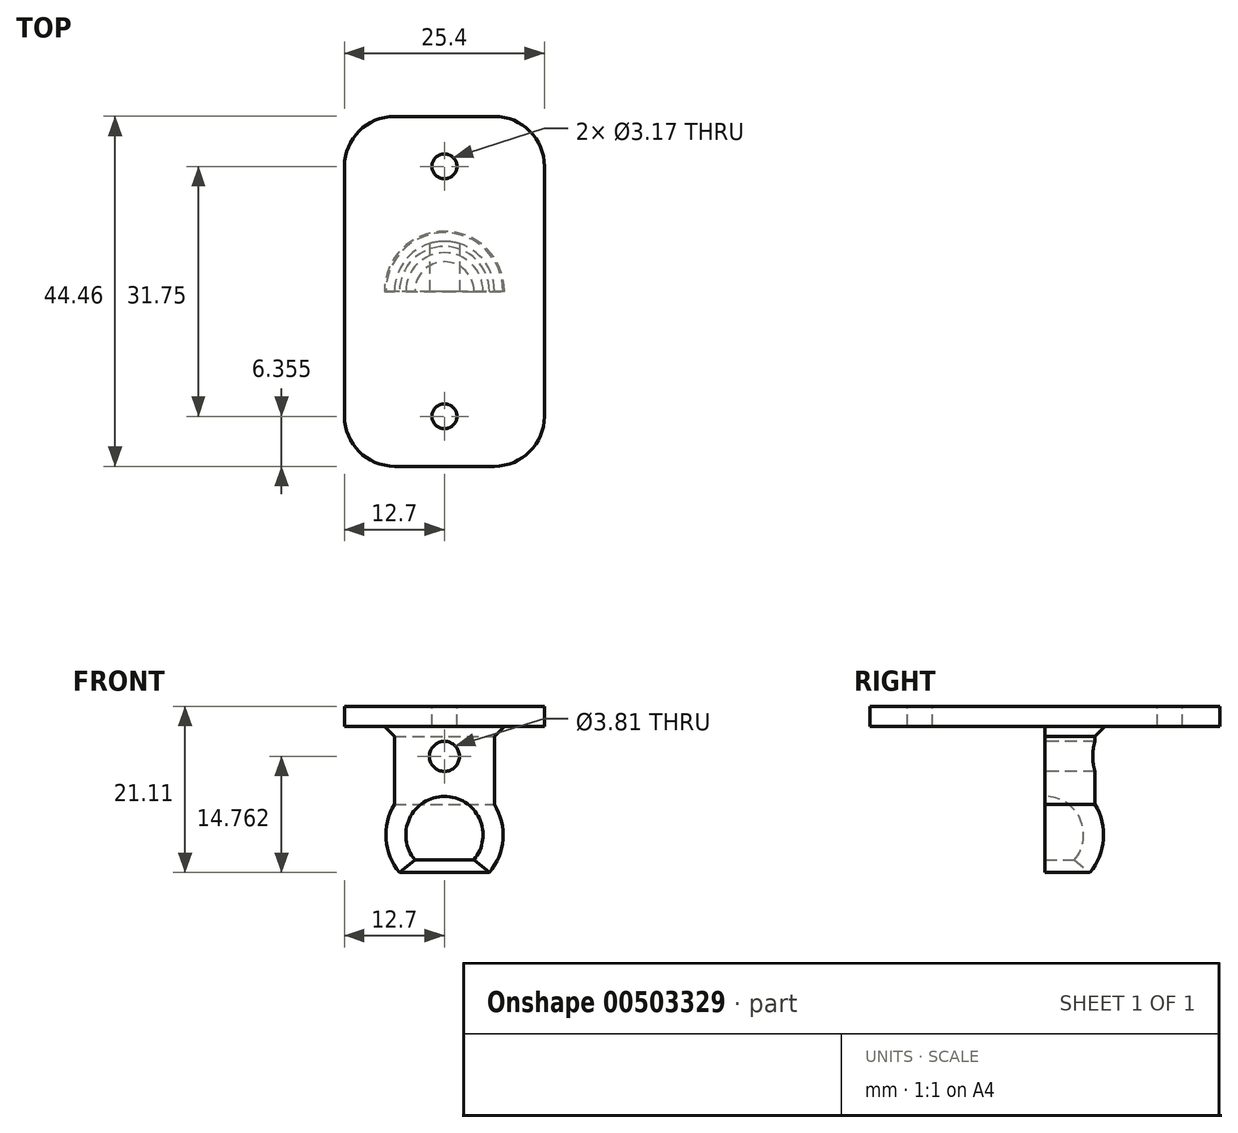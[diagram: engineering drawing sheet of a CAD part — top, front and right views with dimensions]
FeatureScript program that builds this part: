
annotation { "Feature Type Name" : "Feature", "Feature Type Description" : "" }
export const myFeature = defineFeature(function(context is Context, id is Id, definition is map)
    precondition{}
    {
        {
            var Q0;
            Q0=qCreatedBy(makeId("Front.planeOp"),FACE);
            var sketch = newSketch(context, id + "F0", { "sketchPlane" : qUnion([Q0])});
            skArc(sketch, "E0", {"start": v(3.76, -3.15) * mm, "mid": v(4.44, 2.07) * mm, "end": v(0, 4.9) * mm});
            skArc(sketch, "E1.0", {"start": v(5.7, -4.78) * mm, "mid": v(7.42, -0.56) * mm, "end": v(6.35, 3.88) * mm});
            skLineSegment(sketch, "E2", {"start": v(0, 4.9) * mm, "end": v(0, 7.44) * mm});
            skLineSegment(sketch, "E3.top", {"start": v(0, 13.8) * mm, "end": v(6.35, 13.8) * mm});
            skLineSegment(sketch, "E3.left", {"start": v(0, 7.44) * mm, "end": v(0, 13.8) * mm});
            skLineSegment(sketch, "E3.right", {"start": v(6.35, 7.3) * mm, "end": v(6.35, 12.52) * mm});
            skLineSegment(sketch, "E4", {"start": v(6.35, 7.3) * mm, "end": v(6.35, 3.88) * mm});
            skLineSegment(sketch, "E5", {"start": v(3.76, -3.15) * mm, "end": v(5.7, -4.78) * mm});
            skLineSegment(sketch, "E6", {"start": v(6.35, 13.8) * mm, "end": v(7.62, 13.8) * mm});
            skLineSegment(sketch, "E7", {"start": v(7.62, 13.8) * mm, "end": v(6.35, 12.52) * mm});
            skSolve(sketch);
        }
        {
            var Q0;
            Q0=makeQuery(id+"F0.imprint","IMPRINT",FACE,{"disambiguationData":[TD([[makeQuery(id+"F0.imprint","IMPRINT",EDGE,{"derivedFrom":sQuery(id+"F0.wireOp",EDGE,"E0")}),-1.0]])]});
            var Q1;
            Q1=sQuery(id+"F0.wireOp",EDGE,"E3.left");
            revolve(context, id + "F1", {"entities" : qUnion([Q0]), "axis" : qUnion([Q1]), "revolveType" : RevolveType.ONE_DIRECTION, "angle" : 180 * degree});
        }
        {
            var Q0;
            Q0=makeQuery(id+"F1.opRevolve","CAP_FACE",FACE,{"disambiguationData":[OSD([sQuery(id+"F0.wireOp",EDGE,"E0"),sQuery(id+"F0.wireOp",EDGE,"E1.0"),sQuery(id+"F0.wireOp",EDGE,"E2"),sQuery(id+"F0.wireOp",EDGE,"E3.top"),sQuery(id+"F0.wireOp",EDGE,"E3.left"),sQuery(id+"F0.wireOp",EDGE,"E3.right"),sQuery(id+"F0.wireOp",EDGE,"E4"),sQuery(id+"F0.wireOp",EDGE,"E5")])],"isStart":true});
            var sketch = newSketch(context, id + "F2", { "sketchPlane" : qUnion([Q0])});
            skSolve(sketch);
        }
        {
            var Q0;
            Q0=makeQuery(id+"F2.imprint","IMPRINT",FACE,{"disambiguationData":[TD([[makeQuery(id+"F2.imprint","IMPRINT",EDGE,{"derivedFrom":makeQuery(id+"F1.opRevolve","CAP_EDGE",EDGE,{"disambiguationData":[OSD([sQuery(id+"F0.wireOp",EDGE,"E0")])],"isStart":true})}),1.0]])]});
            var sketch = newSketch(context, id + "F3", { "sketchPlane" : qUnion([Q0])});
            skCircle(sketch, "E8", {"center": v(0, 9.98) * mm, "radius": 1.9 * mm});
            skSolve(sketch);
        }
        {
            var Q0;
            Q0=makeQuery(id+"F3.imprint","IMPRINT",FACE,{"disambiguationData":[TD([[makeQuery(id+"F3.imprint","IMPRINT",EDGE,{"derivedFrom":sQuery(id+"F3.wireOp",EDGE,"E8")}),1.0]])]});
            extrude(context, id + "F4", {"entities" : qUnion([Q0]), "operationType" : NewBodyOperationType.REMOVE, "endBound" : BoundingType.THROUGH_ALL, "oppositeDirection" : true, "depth" : 25.4 * mm});
        }
        {
            var Q0;
            Q0=makeQuery(id+"F1.opRevolve","SWEPT_FACE",FACE,{"disambiguationData":[OSD([sQuery(id+"F0.wireOp",EDGE,"E3.top")])]});
            var sketch = newSketch(context, id + "F5", { "sketchPlane" : qUnion([Q0])});
            skLineSegment(sketch, "E9.bottom", {"start": v(-12.7, 22.22) * mm, "end": v(12.7, 22.23) * mm});
            skLineSegment(sketch, "E9.top", {"start": v(-12.7, -22.22) * mm, "end": v(12.7, -22.22) * mm});
            skLineSegment(sketch, "E9.left", {"start": v(-12.7, 22.22) * mm, "end": v(-12.7, -22.22) * mm});
            skLineSegment(sketch, "E9.right", {"start": v(12.7, 22.23) * mm, "end": v(12.7, -22.22) * mm});
            skSolve(sketch);
        }
        {
            var Q0;
            Q0=makeQuery(id+"F5.imprint","IMPRINT",FACE,{"disambiguationData":[TD([[makeQuery(id+"F5.imprint","IMPRINT",EDGE,{"derivedFrom":sQuery(id+"F5.wireOp",EDGE,"E9.bottom")}),-1.0]])]});
            var Q1;
            {var subQ0=sQuery(id+"F0.wireOp",EDGE,"E3.top");Q1=makeQuery(id+"F5.imprint","IMPRINT",FACE,{"disambiguationData":[TD([[makeQuery(id+"F5.imprint","IMPRINT",EDGE,{"derivedFrom":makeQuery(id+"F1.opRevolve","CAP_EDGE",EDGE,{"disambiguationData":[OSD([subQ0])],"isStart":true})}),-1.0]])]});}
            extrude(context, id + "F6", {"entities" : qUnion([Q0, Q1]), "depth" : 2.54 * mm});
        }
        {
            var Q0;
            Q0=makeQuery(id+"F6.opExtrude","SWEPT_EDGE",EDGE,{"disambiguationData":[OSD([sQuery(id+"F5.wireOp",EDGE,"E9.bottom"),sQuery(id+"F5.wireOp",EDGE,"E9.right")])]});
            var Q1;
            Q1=makeQuery(id+"F6.opExtrude","SWEPT_EDGE",EDGE,{"disambiguationData":[OSD([sQuery(id+"F5.wireOp",EDGE,"E9.bottom"),sQuery(id+"F5.wireOp",EDGE,"E9.left")])]});
            var Q2;
            Q2=makeQuery(id+"F6.opExtrude","SWEPT_EDGE",EDGE,{"disambiguationData":[OSD([sQuery(id+"F5.wireOp",EDGE,"E9.top"),sQuery(id+"F5.wireOp",EDGE,"E9.left")])]});
            var Q3;
            Q3=makeQuery(id+"F6.opExtrude","SWEPT_EDGE",EDGE,{"disambiguationData":[OSD([sQuery(id+"F5.wireOp",EDGE,"E9.top"),sQuery(id+"F5.wireOp",EDGE,"E9.right")])]});
            fillet(context, id + "F7", {"entities" : qUnion([Q0, Q1, Q2, Q3]), "radius" : 6.35 * mm, "tangentPropagation" : true, "allowEdgeOverflow" : false});
        }
        {
            var Q0;
            Q0=makeQuery(id+"F6.opExtrude","CAP_FACE",FACE,{"disambiguationData":[OSD([sQuery(id+"F5.wireOp",EDGE,"E9.bottom"),sQuery(id+"F5.wireOp",EDGE,"E9.top"),sQuery(id+"F5.wireOp",EDGE,"E9.left"),sQuery(id+"F5.wireOp",EDGE,"E9.right")])],"isStart":false});
            var sketch = newSketch(context, id + "F8", { "sketchPlane" : qUnion([Q0])});
            skCircle(sketch, "E10", {"center": v(0, 15.88) * mm, "radius": 1.59 * mm});
            skCircle(sketch, "E11", {"center": v(0, -15.87) * mm, "radius": 1.59 * mm});
            skSolve(sketch);
        }
        {
            var Q0;
            Q0=makeQuery(id+"F8.imprint","IMPRINT",FACE,{"disambiguationData":[TD([[makeQuery(id+"F8.imprint","IMPRINT",EDGE,{"derivedFrom":sQuery(id+"F8.wireOp",EDGE,"E10")}),1.0]])]});
            var Q1;
            Q1=makeQuery(id+"F8.imprint","IMPRINT",FACE,{"disambiguationData":[TD([[makeQuery(id+"F8.imprint","IMPRINT",EDGE,{"derivedFrom":sQuery(id+"F8.wireOp",EDGE,"E11")}),1.0]])]});
            extrude(context, id + "F9", {"entities" : qUnion([Q0, Q1]), "operationType" : NewBodyOperationType.REMOVE, "endBound" : BoundingType.THROUGH_ALL, "oppositeDirection" : true, "depth" : 25.4 * mm});
        }
    });
